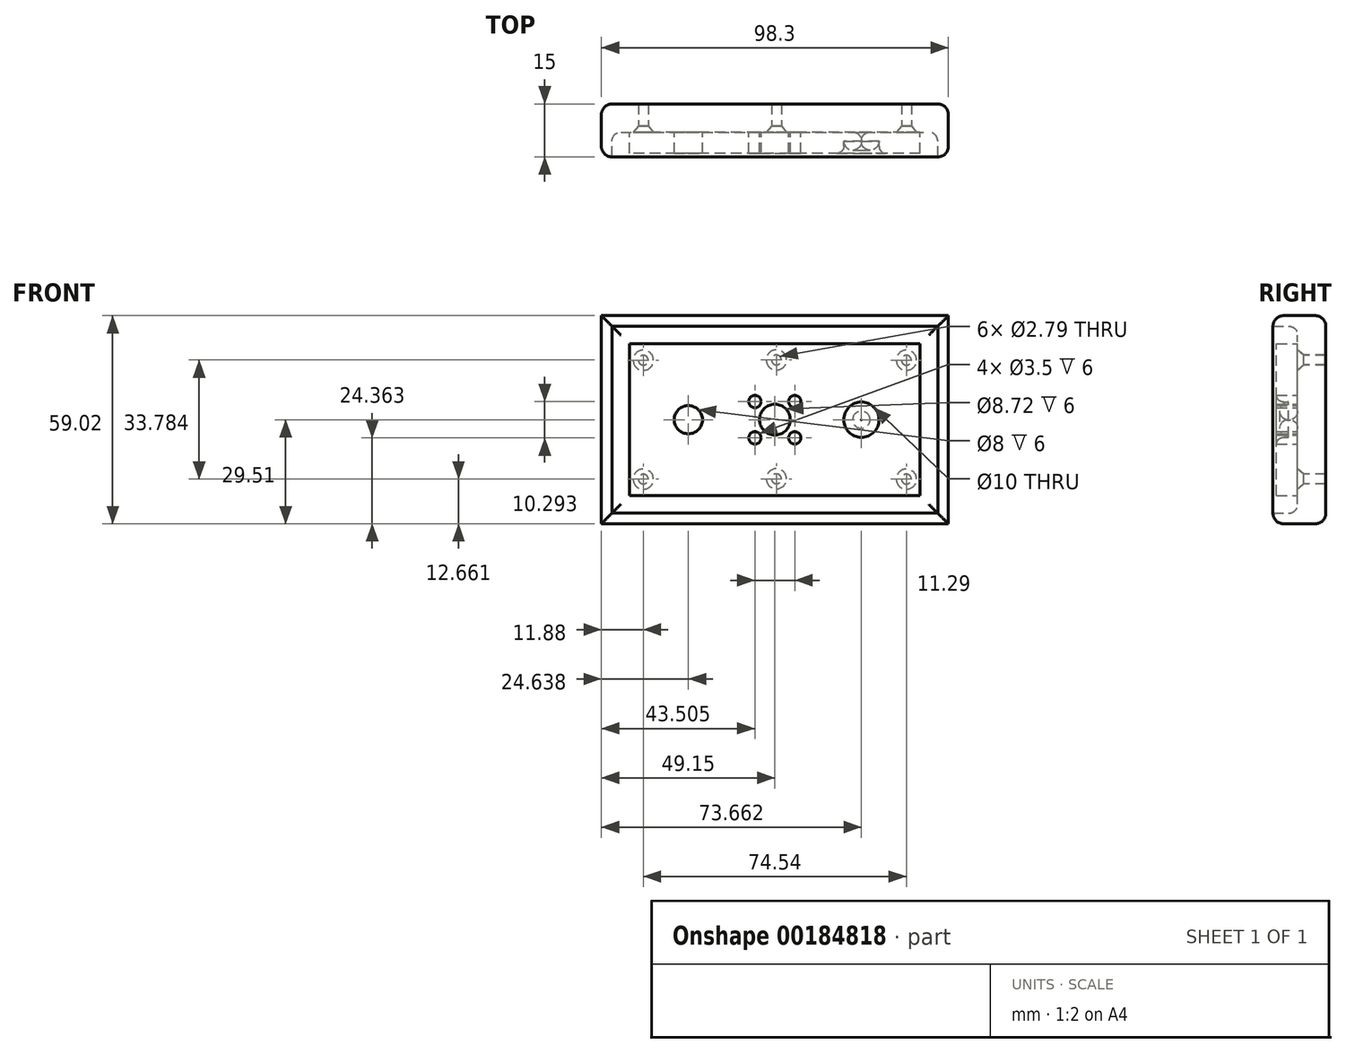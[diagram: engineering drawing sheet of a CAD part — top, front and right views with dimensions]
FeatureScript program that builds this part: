
annotation { "Feature Type Name" : "Feature", "Feature Type Description" : "" }
export const myFeature = defineFeature(function(context is Context, id is Id, definition is map)
    precondition{}
    {
        {
            var Q0;
            Q0=qCreatedBy(makeId("Front.planeOp"),FACE);
            var sketch = newSketch(context, id + "F0", { "sketchPlane" : qUnion([Q0])});
            skLineSegment(sketch, "E0.bottom", {"start": v(46.15, 26.5) * mm, "end": v(-46.15, 26.5) * mm});
            skLineSegment(sketch, "E0.top", {"start": v(46.15, -26.5) * mm, "end": v(-46.15, -26.5) * mm});
            skLineSegment(sketch, "E0.left", {"start": v(46.15, 26.5) * mm, "end": v(46.15, -26.5) * mm});
            skLineSegment(sketch, "E0.right", {"start": v(-46.15, 26.5) * mm, "end": v(-46.15, -26.5) * mm});
            skPoint(sketch, "E0.middle", {"position": v(0, 0) * mm});
            skLineSegment(sketch, "E1.0", {"start": v(49.15, 29.5) * mm, "end": v(-49.15, 29.5) * mm});
            skLineSegment(sketch, "E1.1", {"start": v(49.15, 29.5) * mm, "end": v(49.15, -29.5) * mm});
            skLineSegment(sketch, "E1.2", {"start": v(49.15, -29.5) * mm, "end": v(-49.15, -29.5) * mm});
            skLineSegment(sketch, "E1.3", {"start": v(-49.15, 29.5) * mm, "end": v(-49.15, -29.5) * mm});
            skSolve(sketch);
        }
        {
            var Q0;
            Q0=makeQuery(id+"F0.imprint","IMPRINT",FACE,{"disambiguationData":[TD([[makeQuery(id+"F0.imprint","IMPRINT",EDGE,{"derivedFrom":sQuery(id+"F0.wireOp",EDGE,"E0.bottom")}),1.0]])]});
            var Q1;
            Q1=makeQuery(id+"F0.imprint","IMPRINT",FACE,{"disambiguationData":[TD([[makeQuery(id+"F0.imprint","IMPRINT",EDGE,{"derivedFrom":sQuery(id+"F0.wireOp",EDGE,"E0.bottom")}),-1.0]])]});
            extrude(context, id + "F1", {"entities" : qUnion([Q0, Q1]), "depth" : 8 * mm});
        }
        {
            var Q0;
            Q0 = qSketchRegion(id + "F0", true);
            extrude(context, id + "F2", {"entities" : qUnion([Q0]), "operationType" : NewBodyOperationType.ADD, "depth" : 15 * mm});
        }
        {
            var Q0;
            Q0=makeQuery(id+"F1.opExtrude","CAP_FACE",FACE,{"disambiguationData":[OSD([sQuery(id+"F0.wireOp",EDGE,"E1.0"),sQuery(id+"F0.wireOp",EDGE,"E1.1"),sQuery(id+"F0.wireOp",EDGE,"E1.2"),sQuery(id+"F0.wireOp",EDGE,"E1.3")])],"isStart":false});
            var sketch = newSketch(context, id + "F3", { "sketchPlane" : qUnion([Q0])});
            skCircle(sketch, "E2", {"center": v(0, 0) * mm, "radius": 4.36 * mm});
            skCircle(sketch, "E3", {"center": v(-5.64, 5.15) * mm, "radius": 1.75 * mm});
            skCircle(sketch, "E4.MirrorC", {"center": v(5.64, 5.15) * mm, "radius": 1.75 * mm});
            skCircle(sketch, "E5.MirrorC", {"center": v(-5.64, -5.15) * mm, "radius": 1.75 * mm});
            skCircle(sketch, "E6.MirrorC", {"center": v(5.64, -5.15) * mm, "radius": 1.75 * mm});
            skLineSegment(sketch, "E7.0", {"start": v(41.15, 21.5) * mm, "end": v(-41.15, 21.5) * mm});
            skLineSegment(sketch, "E7.1", {"start": v(41.15, -21.5) * mm, "end": v(41.15, 21.5) * mm});
            skLineSegment(sketch, "E7.2", {"start": v(-41.15, -21.5) * mm, "end": v(41.15, -21.5) * mm});
            skLineSegment(sketch, "E7.3", {"start": v(-41.15, 21.5) * mm, "end": v(-41.15, -21.5) * mm});
            skCircle(sketch, "E8", {"center": v(-24.51, 0) * mm, "radius": 4 * mm});
            skCircle(sketch, "E9.0", {"center": v(-24.51, 0) * mm, "radius": 5 * mm});
            skCircle(sketch, "E10.MirrorC", {"center": v(24.51, 0) * mm, "radius": 5 * mm});
            skCircle(sketch, "E11.MirrorC", {"center": v(24.51, 0) * mm, "radius": 4 * mm});
            skSolve(sketch);
        }
        {
            var Q0;
            Q0=makeQuery(id+"F3.imprint","IMPRINT",FACE,{"disambiguationData":[TD([[makeQuery(id+"F3.imprint","IMPRINT",EDGE,{"derivedFrom":sQuery(id+"F3.wireOp",EDGE,"E8")}),-1.0]])]});
            var Q1;
            Q1=makeQuery(id+"F3.imprint","IMPRINT",FACE,{"disambiguationData":[TD([[makeQuery(id+"F3.imprint","IMPRINT",EDGE,{"derivedFrom":sQuery(id+"F3.wireOp",EDGE,"E10.MirrorC")}),-1.0]])]});
            extrude(context, id + "F4", {"entities" : qUnion([Q0, Q1]), "operationType" : NewBodyOperationType.ADD, "depth" : 6 * mm});
        }
        {
            var Q0;
            Q0=makeQuery(id+"F4.opExtrude","CAP_EDGE",EDGE,{"disambiguationData":[OSD([sQuery(id+"F3.wireOp",EDGE,"E9.0")])],"isStart":true});
            var Q1;
            Q1=makeQuery(id+"F4.opExtrude","CAP_EDGE",EDGE,{"disambiguationData":[OSD([sQuery(id+"F3.wireOp",EDGE,"E10.MirrorC")])],"isStart":true});
            var Q2;
            Q2=makeQuery(id+"F2.boolean.opBoolean","INTERSECT",EDGE,{"derivedFrom":[makeQuery(id+"F1.opExtrude","CAP_FACE",FACE,{"disambiguationData":[OSD([sQuery(id+"F0.wireOp",EDGE,"E1.0"),sQuery(id+"F0.wireOp",EDGE,"E1.1"),sQuery(id+"F0.wireOp",EDGE,"E1.2"),sQuery(id+"F0.wireOp",EDGE,"E1.3")])],"isStart":false}),makeQuery(id+"F2.opExtrude","SWEPT_FACE",FACE,{"disambiguationData":[OSD([sQuery(id+"F0.wireOp",EDGE,"E0.top")])]})]});
            var Q3;
            Q3=makeQuery(id+"F2.boolean.opBoolean","INTERSECT",EDGE,{"derivedFrom":[makeQuery(id+"F1.opExtrude","CAP_FACE",FACE,{"disambiguationData":[OSD([sQuery(id+"F0.wireOp",EDGE,"E1.0"),sQuery(id+"F0.wireOp",EDGE,"E1.1"),sQuery(id+"F0.wireOp",EDGE,"E1.2"),sQuery(id+"F0.wireOp",EDGE,"E1.3")])],"isStart":false}),makeQuery(id+"F2.opExtrude","SWEPT_FACE",FACE,{"disambiguationData":[OSD([sQuery(id+"F0.wireOp",EDGE,"E0.left")])]})]});
            var Q4;
            Q4=makeQuery(id+"F2.boolean.opBoolean","INTERSECT",EDGE,{"derivedFrom":[makeQuery(id+"F1.opExtrude","CAP_FACE",FACE,{"disambiguationData":[OSD([sQuery(id+"F0.wireOp",EDGE,"E1.0"),sQuery(id+"F0.wireOp",EDGE,"E1.1"),sQuery(id+"F0.wireOp",EDGE,"E1.2"),sQuery(id+"F0.wireOp",EDGE,"E1.3")])],"isStart":false}),makeQuery(id+"F2.opExtrude","SWEPT_FACE",FACE,{"disambiguationData":[OSD([sQuery(id+"F0.wireOp",EDGE,"E0.right")])]})]});
            var Q5;
            Q5=makeQuery(id+"F2.boolean.opBoolean","INTERSECT",EDGE,{"derivedFrom":[makeQuery(id+"F1.opExtrude","CAP_FACE",FACE,{"disambiguationData":[OSD([sQuery(id+"F0.wireOp",EDGE,"E1.0"),sQuery(id+"F0.wireOp",EDGE,"E1.1"),sQuery(id+"F0.wireOp",EDGE,"E1.2"),sQuery(id+"F0.wireOp",EDGE,"E1.3")])],"isStart":false}),makeQuery(id+"F2.opExtrude","SWEPT_FACE",FACE,{"disambiguationData":[OSD([sQuery(id+"F0.wireOp",EDGE,"E0.bottom")])]})]});
            fillet(context, id + "F5", {"entities" : qUnion([Q0, Q1, Q2, Q3, Q4, Q5]), "radius" : 2.54 * mm, "tangentPropagation" : true, "allowEdgeOverflow" : false});
        }
        {
            var Q0;
            Q0=makeQuery(id+"F1.opExtrude","CAP_EDGE",EDGE,{"disambiguationData":[OSD([sQuery(id+"F0.wireOp",EDGE,"E1.0")])],"isStart":true});
            var Q1;
            Q1=makeQuery(id+"F1.opExtrude","CAP_EDGE",EDGE,{"disambiguationData":[OSD([sQuery(id+"F0.wireOp",EDGE,"E1.1")])],"isStart":true});
            var Q2;
            Q2=makeQuery(id+"F1.opExtrude","CAP_EDGE",EDGE,{"disambiguationData":[OSD([sQuery(id+"F0.wireOp",EDGE,"E1.2")])],"isStart":true});
            var Q3;
            Q3=makeQuery(id+"F1.opExtrude","CAP_EDGE",EDGE,{"disambiguationData":[OSD([sQuery(id+"F0.wireOp",EDGE,"E1.3")])],"isStart":true});
            fillet(context, id + "F6", {"entities" : qUnion([Q0, Q1, Q2, Q3]), "radius" : 3 * mm, "tangentPropagation" : true, "allowEdgeOverflow" : false});
        }
        {
            var Q0;
            Q0=makeQuery(id+"F2.opExtrude","CAP_EDGE",EDGE,{"disambiguationData":[OSD([sQuery(id+"F0.wireOp",EDGE,"E1.2")])],"isStart":false});
            var Q1;
            Q1=makeQuery(id+"F2.opExtrude","CAP_EDGE",EDGE,{"disambiguationData":[OSD([sQuery(id+"F0.wireOp",EDGE,"E1.1")])],"isStart":false});
            var Q2;
            Q2=makeQuery(id+"F2.opExtrude","CAP_EDGE",EDGE,{"disambiguationData":[OSD([sQuery(id+"F0.wireOp",EDGE,"E1.3")])],"isStart":false});
            var Q3;
            Q3=makeQuery(id+"F2.opExtrude","CAP_EDGE",EDGE,{"disambiguationData":[OSD([sQuery(id+"F0.wireOp",EDGE,"E1.0")])],"isStart":false});
            fillet(context, id + "F7", {"entities" : qUnion([Q0, Q1, Q2, Q3]), "radius" : 3 * mm, "tangentPropagation" : true, "allowEdgeOverflow" : false});
        }
        {
            var Q0;
            Q0=makeQuery(id+"F4.opExtrude","CAP_EDGE",EDGE,{"disambiguationData":[OSD([sQuery(id+"F3.wireOp",EDGE,"E10.MirrorC")])],"isStart":false});
            var Q1;
            Q1=makeQuery(id+"F4.opExtrude","CAP_EDGE",EDGE,{"disambiguationData":[OSD([sQuery(id+"F3.wireOp",EDGE,"E9.0")])],"isStart":false});
            fillet(context, id + "F8", {"entities" : qUnion([Q0, Q1]), "radius" : 2 * mm, "tangentPropagation" : true, "allowEdgeOverflow" : false});
        }
        {
            var Q0;
            Q0=makeQuery(id+"F4.boolean.opBoolean","SPLIT",FACE,{"disambiguationData":[TD([makeQuery(id+"F2.opExtrude","SWEPT_FACE",FACE,{"disambiguationData":[OSD([sQuery(id+"F0.wireOp",EDGE,"E0.bottom")])]})])],"derivedFrom":makeQuery(id+"F1.opExtrude","CAP_FACE",FACE,{"disambiguationData":[OSD([sQuery(id+"F0.wireOp",EDGE,"E1.0"),sQuery(id+"F0.wireOp",EDGE,"E1.1"),sQuery(id+"F0.wireOp",EDGE,"E1.2"),sQuery(id+"F0.wireOp",EDGE,"E1.3")])],"isStart":false})});
            var sketch = newSketch(context, id + "F9", { "sketchPlane" : qUnion([Q0])});
            skCircle(sketch, "E12", {"center": v(37.27, 16.85) * mm, "radius": 2.69 * mm});
            skCircle(sketch, "E13.MirrorC", {"center": v(37.27, -16.85) * mm, "radius": 2.69 * mm});
            skCircle(sketch, "E14.MirrorC", {"center": v(-37.27, 16.85) * mm, "radius": 2.69 * mm});
            skCircle(sketch, "E15.MirrorC", {"center": v(-37.27, -16.85) * mm, "radius": 2.69 * mm});
            skCircle(sketch, "E16", {"center": v(0.43, 16.93) * mm, "radius": 2.69 * mm});
            skCircle(sketch, "E17.MirrorC", {"center": v(0.43, -16.76) * mm, "radius": 2.69 * mm});
            skSolve(sketch);
        }
        {
            var Q0;
            Q0=sQuery(id+"F9.wireOp",VERTEX,"E12.center");
            var Q1;
            Q1=sQuery(id+"F9.wireOp",VERTEX,"E13.MirrorC.center");
            var Q2;
            Q2=sQuery(id+"F9.wireOp",VERTEX,"E17.MirrorC.center");
            var Q3;
            Q3=sQuery(id+"F9.wireOp",VERTEX,"E16.center");
            var Q4;
            Q4=sQuery(id+"F9.wireOp",VERTEX,"E14.MirrorC.center");
            var Q5;
            Q5=sQuery(id+"F9.wireOp",VERTEX,"E15.MirrorC.center");
            var Q6;
            Q6=makeQuery(id+"F1.opExtrude","SWEPT_BODY",BODY,{"disambiguationData":[OSD([sQuery(id+"F0.wireOp",EDGE,"E1.0"),sQuery(id+"F0.wireOp",EDGE,"E1.1"),sQuery(id+"F0.wireOp",EDGE,"E1.2"),sQuery(id+"F0.wireOp",EDGE,"E1.3")])]});
            hole(context, id + "F10", {"style" : HoleStyle.C_SINK, "endStyle" : HoleEndStyle.THROUGH, "standardTappedOrClearance" : lookupTablePath({ "standard" : "ANSI", "fit" : "Normal (ASME)", "size" : "#3", "type" : "Clearance" }), "standardBlindInLast" : lookupTablePath({ "fit" : "Free", "standard" : "ANSI", "size" : "#3", "type" : "Clearance" }), "holeDiameter" : 2.8 * mm, "cSinkDiameter" : 5.74 * mm, "cSinkAngle" : 82 * degree, "startFromSketch" : true, "locations" : qUnion([Q0, Q1, Q2, Q3, Q4, Q5]), "scope" : qUnion([Q6]), "isTappedThrough" : true});
        }
    });
